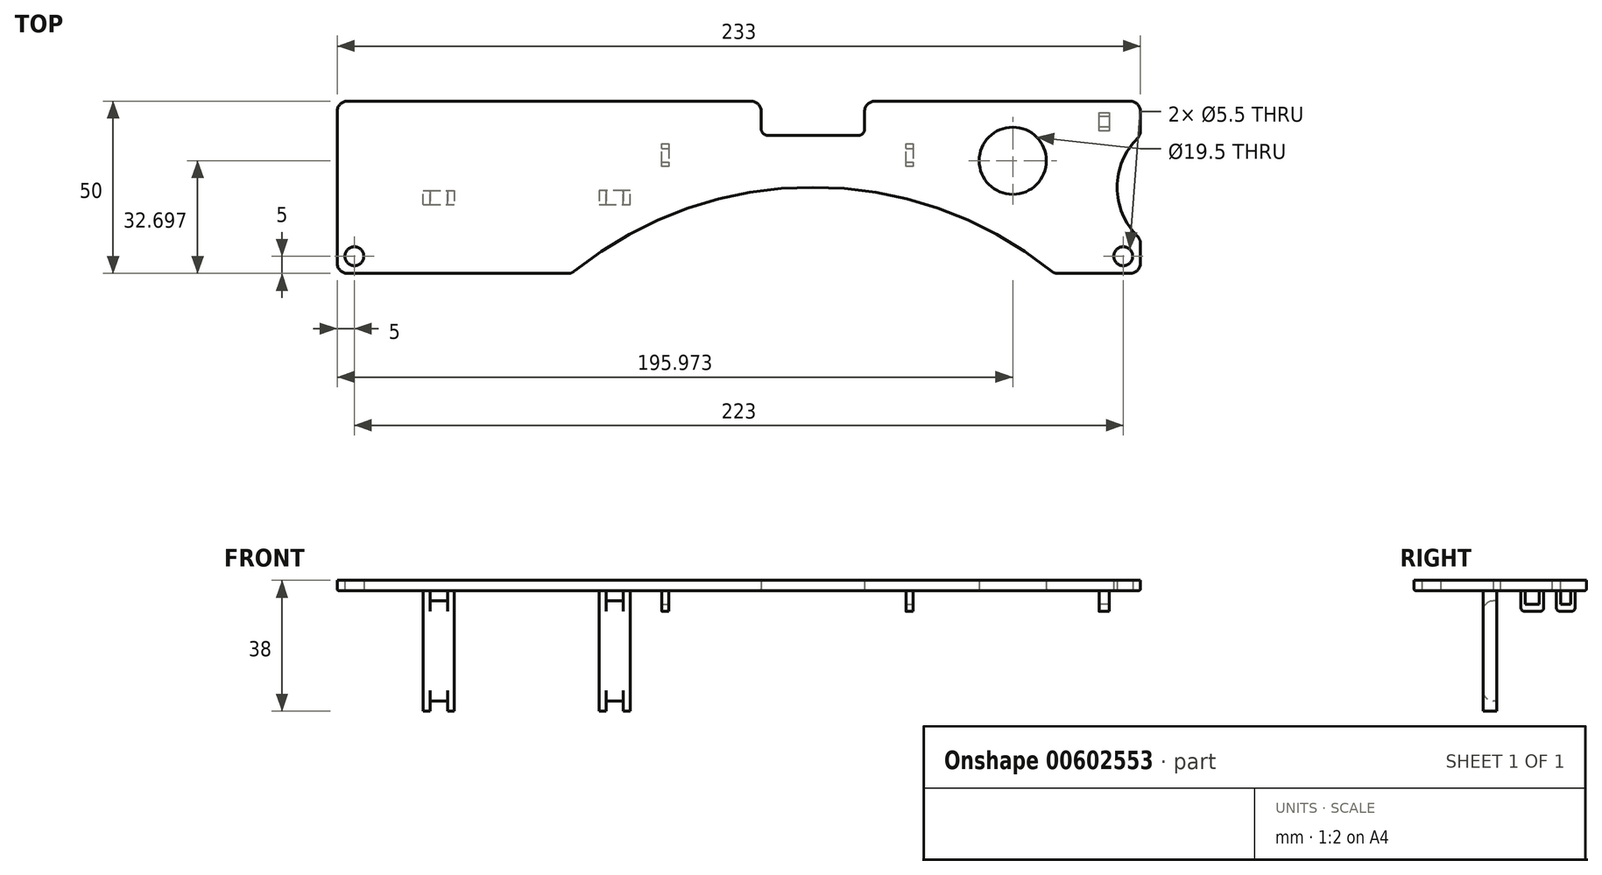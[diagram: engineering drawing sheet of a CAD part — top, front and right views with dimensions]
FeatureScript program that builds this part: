
annotation { "Feature Type Name" : "Feature", "Feature Type Description" : "" }
export const myFeature = defineFeature(function(context is Context, id is Id, definition is map)
    precondition{}
    {
        {
            var Q0;
            Q0=qCreatedBy(makeId("Top.planeOp"),FACE);
            var sketch = newSketch(context, id + "F0", { "sketchPlane" : qUnion([Q0])});
            skLineSegment(sketch, "E0", {"start": v(0, 40) * mm, "end": v(13, 40) * mm});
            skLineSegment(sketch, "E1", {"start": v(15, 42) * mm, "end": v(15, 47) * mm});
            skLineSegment(sketch, "E2", {"start": v(18, 50) * mm, "end": v(85, 50) * mm});
            skLineSegment(sketch, "E3", {"start": v(85, 50) * mm, "end": v(92, 50) * mm});
            skLineSegment(sketch, "E4", {"start": v(92, 0) * mm, "end": v(85, 0) * mm});
            skLineSegment(sketch, "E5", {"start": v(85, 0) * mm, "end": v(71.06, 0) * mm});
            skLineSegment(sketch, "E6", {"start": v(0, 40) * mm, "end": v(-13, 40) * mm});
            skLineSegment(sketch, "E7", {"start": v(-15, 42) * mm, "end": v(-15, 47) * mm});
            skLineSegment(sketch, "E8", {"start": v(-18, 50) * mm, "end": v(-128, 50) * mm});
            skLineSegment(sketch, "E9", {"start": v(-128, 50) * mm, "end": v(-135, 50) * mm});
            skLineSegment(sketch, "E10", {"start": v(-138, 47) * mm, "end": v(-138, 3) * mm});
            skLineSegment(sketch, "E11", {"start": v(-135, 0) * mm, "end": v(-128, 0) * mm});
            skLineSegment(sketch, "E12", {"start": v(-128, 0) * mm, "end": v(-71.06, 0) * mm});
            skArc(sketch, "E13", {"start": v(69.19, 0.66) * mm, "mid": v(0, 25) * mm, "end": v(-69.19, 0.66) * mm});
            skCircle(sketch, "E14", {"center": v(-133, 5) * mm, "radius": 2.75 * mm});
            skCircle(sketch, "E15", {"center": v(90, 5) * mm, "radius": 2.75 * mm});
            skLineSegment(sketch, "E16", {"start": v(95, 3) * mm, "end": v(95, 8.7) * mm});
            skLineSegment(sketch, "E17", {"start": v(95, 47) * mm, "end": v(95, 41.3) * mm});
            skArc(sketch, "E18", {"start": v(94.12, 39.17) * mm, "mid": v(88.23, 25) * mm, "end": v(94.12, 10.83) * mm});
            skPoint(sketch, "E19.visualSharp", {"position": v(-138, 0) * mm});
            skArc(sketch, "E19.filletArc", {"start": v(-138, 3) * mm, "mid": v(-137.12, 0.88) * mm, "end": v(-135, 0) * mm});
            skPoint(sketch, "E20.visualSharp", {"position": v(-138, 50) * mm});
            skArc(sketch, "E20.filletArc", {"start": v(-135, 50) * mm, "mid": v(-137.12, 49.12) * mm, "end": v(-138, 47) * mm});
            skPoint(sketch, "E21.visualSharp", {"position": v(-15, 50) * mm});
            skArc(sketch, "E21.filletArc", {"start": v(-15, 47) * mm, "mid": v(-15.88, 49.12) * mm, "end": v(-18, 50) * mm});
            skPoint(sketch, "E22.visualSharp", {"position": v(15, 50) * mm});
            skArc(sketch, "E22.filletArc", {"start": v(18, 50) * mm, "mid": v(15.88, 49.12) * mm, "end": v(15, 47) * mm});
            skPoint(sketch, "E23.visualSharp", {"position": v(95, 50) * mm});
            skArc(sketch, "E23.filletArc", {"start": v(95, 47) * mm, "mid": v(94.12, 49.12) * mm, "end": v(92, 50) * mm});
            skPoint(sketch, "E24.visualSharp", {"position": v(95, 40) * mm});
            skArc(sketch, "E24.filletArc", {"start": v(94.12, 39.17) * mm, "mid": v(94.77, 40.15) * mm, "end": v(95, 41.3) * mm});
            skPoint(sketch, "E25.visualSharp", {"position": v(95, 10) * mm});
            skArc(sketch, "E25.filletArc", {"start": v(95, 8.7) * mm, "mid": v(94.77, 9.85) * mm, "end": v(94.12, 10.83) * mm});
            skPoint(sketch, "E26.visualSharp", {"position": v(95, 0) * mm});
            skArc(sketch, "E26.filletArc", {"start": v(92, 0) * mm, "mid": v(94.12, 0.88) * mm, "end": v(95, 3) * mm});
            skPoint(sketch, "E27.visualSharp", {"position": v(70, 0) * mm});
            skArc(sketch, "E27.filletArc", {"start": v(69.19, 0.66) * mm, "mid": v(70.07, 0.17) * mm, "end": v(71.06, 0) * mm});
            skPoint(sketch, "E28.visualSharp", {"position": v(-70, 0) * mm});
            skArc(sketch, "E28.filletArc", {"start": v(-71.06, 0) * mm, "mid": v(-70.07, 0.17) * mm, "end": v(-69.19, 0.66) * mm});
            skPoint(sketch, "E29.visualSharp", {"position": v(-15, 40) * mm});
            skArc(sketch, "E29.filletArc", {"start": v(-15, 42) * mm, "mid": v(-14.41, 40.59) * mm, "end": v(-13, 40) * mm});
            skPoint(sketch, "E30.visualSharp", {"position": v(15, 40) * mm});
            skArc(sketch, "E30.filletArc", {"start": v(13, 40) * mm, "mid": v(14.41, 40.59) * mm, "end": v(15, 42) * mm});
            skCircle(sketch, "E31", {"center": v(57.97, 32.7) * mm, "radius": 9.75 * mm});
            skLineSegment(sketch, "E32", {"start": v(-113, 20) * mm, "end": v(-113, 24) * mm});
            skLineSegment(sketch, "E33", {"start": v(-113, 24) * mm, "end": v(-111, 24) * mm});
            skLineSegment(sketch, "E34", {"start": v(-111, 24) * mm, "end": v(-106, 24) * mm});
            skLineSegment(sketch, "E35", {"start": v(-106, 24) * mm, "end": v(-104, 24) * mm});
            skLineSegment(sketch, "E36", {"start": v(-104, 24) * mm, "end": v(-104, 20) * mm});
            skLineSegment(sketch, "E37", {"start": v(-53, 20) * mm, "end": v(-53, 24) * mm});
            skLineSegment(sketch, "E38", {"start": v(-53, 24) * mm, "end": v(-55, 24) * mm});
            skLineSegment(sketch, "E39", {"start": v(-55, 24) * mm, "end": v(-60, 24) * mm});
            skLineSegment(sketch, "E40", {"start": v(-60, 24) * mm, "end": v(-62, 24) * mm});
            skLineSegment(sketch, "E41", {"start": v(-62, 24) * mm, "end": v(-62, 20) * mm});
            skLineSegment(sketch, "E42", {"start": v(-62, 20) * mm, "end": v(-53, 20) * mm});
            skLineSegment(sketch, "E43", {"start": v(-55, 24) * mm, "end": v(-55, 20) * mm});
            skLineSegment(sketch, "E44", {"start": v(-60, 24) * mm, "end": v(-60, 20) * mm});
            skLineSegment(sketch, "E45", {"start": v(-113, 20) * mm, "end": v(-104, 20) * mm});
            skLineSegment(sketch, "E46", {"start": v(-106, 24) * mm, "end": v(-106, 20) * mm});
            skLineSegment(sketch, "E47", {"start": v(-111, 24) * mm, "end": v(-111, 20) * mm});
            skLineSegment(sketch, "E48", {"start": v(27, 31) * mm, "end": v(27, 32.3) * mm});
            skLineSegment(sketch, "E49", {"start": v(-43.79, 31) * mm, "end": v(-43.79, 32.3) * mm});
            skLineSegment(sketch, "E50", {"start": v(-43.79, 32.3) * mm, "end": v(-43.79, 36.3) * mm});
            skLineSegment(sketch, "E51", {"start": v(-43.79, 36.3) * mm, "end": v(-43.79, 37.6) * mm});
            skLineSegment(sketch, "E52", {"start": v(-43.79, 37.6) * mm, "end": v(-41.79, 37.6) * mm});
            skLineSegment(sketch, "E53", {"start": v(27, 32.3) * mm, "end": v(27, 36.3) * mm});
            skLineSegment(sketch, "E54", {"start": v(27, 36.3) * mm, "end": v(27, 37.6) * mm});
            skLineSegment(sketch, "E55", {"start": v(27, 37.6) * mm, "end": v(29, 37.6) * mm});
            skLineSegment(sketch, "E56", {"start": v(29, 37.6) * mm, "end": v(29, 36.3) * mm});
            skLineSegment(sketch, "E57", {"start": v(29, 36.3) * mm, "end": v(29, 32.3) * mm});
            skLineSegment(sketch, "E58", {"start": v(29, 32.3) * mm, "end": v(29, 31) * mm});
            skLineSegment(sketch, "E59", {"start": v(29, 31) * mm, "end": v(27, 31) * mm});
            skLineSegment(sketch, "E60", {"start": v(27, 32.3) * mm, "end": v(29, 32.3) * mm});
            skLineSegment(sketch, "E61", {"start": v(27, 36.3) * mm, "end": v(29, 36.3) * mm});
            skLineSegment(sketch, "E62", {"start": v(-41.79, 37.6) * mm, "end": v(-41.79, 36.3) * mm});
            skLineSegment(sketch, "E63", {"start": v(-41.79, 36.3) * mm, "end": v(-41.79, 32.3) * mm});
            skLineSegment(sketch, "E64", {"start": v(-41.79, 32.3) * mm, "end": v(-41.79, 31) * mm});
            skLineSegment(sketch, "E65", {"start": v(-41.79, 31) * mm, "end": v(-43.79, 31) * mm});
            skLineSegment(sketch, "E66", {"start": v(-43.79, 32.3) * mm, "end": v(-41.79, 32.3) * mm});
            skLineSegment(sketch, "E67", {"start": v(-43.79, 36.3) * mm, "end": v(-41.79, 36.3) * mm});
            skLineSegment(sketch, "E68", {"start": v(86, 41.3) * mm, "end": v(83, 41.3) * mm});
            skLineSegment(sketch, "E69", {"start": v(83, 41.3) * mm, "end": v(83, 42.5) * mm});
            skLineSegment(sketch, "E70", {"start": v(83, 42.5) * mm, "end": v(83, 45.5) * mm});
            skLineSegment(sketch, "E71", {"start": v(83, 45.5) * mm, "end": v(83, 46.7) * mm});
            skLineSegment(sketch, "E72", {"start": v(83, 46.7) * mm, "end": v(86, 46.7) * mm});
            skLineSegment(sketch, "E73", {"start": v(86, 46.7) * mm, "end": v(86, 45.5) * mm});
            skLineSegment(sketch, "E74", {"start": v(86, 45.5) * mm, "end": v(83, 45.5) * mm});
            skLineSegment(sketch, "E75", {"start": v(86, 45.5) * mm, "end": v(86, 42.5) * mm});
            skLineSegment(sketch, "E76", {"start": v(86, 42.5) * mm, "end": v(83, 42.5) * mm});
            skLineSegment(sketch, "E77", {"start": v(86, 42.5) * mm, "end": v(86, 41.3) * mm});
            skLineSegment(sketch, "E78.bottom", {"start": v(-21.5, -115.24) * mm, "end": v(119.92, 26.18) * mm, "construction": true});
            skLineSegment(sketch, "E78.top", {"start": v(-162.92, 26.18) * mm, "end": v(-21.5, 167.6) * mm, "construction": true});
            skLineSegment(sketch, "E78.left", {"start": v(-21.5, -115.24) * mm, "end": v(-162.92, 26.18) * mm, "construction": true});
            skLineSegment(sketch, "E78.right", {"start": v(119.92, 26.18) * mm, "end": v(-21.5, 167.6) * mm, "construction": true});
            skSolve(sketch);
        }
        {
            var Q0;
            Q0=makeQuery(id+"F0.imprint","IMPRINT",FACE,{"disambiguationData":[TD([[makeQuery(id+"F0.imprint","IMPRINT",EDGE,{"derivedFrom":sQuery(id+"F0.wireOp",EDGE,"E0")}),-1.0]])]});
            var Q1;
            Q1=makeQuery(id+"F0.imprint","IMPRINT",FACE,{"disambiguationData":[TD([[makeQuery(id+"F0.imprint","IMPRINT",EDGE,{"derivedFrom":sQuery(id+"F0.wireOp",EDGE,"E34")}),-1.0]])]});
            var Q2;
            {var subQ0=sQuery(id+"F0.wireOp",EDGE,"E32");Q2=makeQuery(id+"F0.imprint","IMPRINT",FACE,{"disambiguationData":[TD([[makeQuery(id+"F0.imprint","IMPRINT",EDGE,{"derivedFrom":subQ0}),-1.0]])]});}
            var Q3;
            Q3=makeQuery(id+"F0.imprint","IMPRINT",FACE,{"disambiguationData":[TD([[makeQuery(id+"F0.imprint","IMPRINT",EDGE,{"derivedFrom":sQuery(id+"F0.wireOp",EDGE,"E35")}),-1.0]])]});
            var Q4;
            Q4=makeQuery(id+"F0.imprint","IMPRINT",FACE,{"disambiguationData":[TD([[makeQuery(id+"F0.imprint","IMPRINT",EDGE,{"derivedFrom":sQuery(id+"F0.wireOp",EDGE,"E39")}),1.0]])]});
            var Q5;
            Q5=makeQuery(id+"F0.imprint","IMPRINT",FACE,{"disambiguationData":[TD([[makeQuery(id+"F0.imprint","IMPRINT",EDGE,{"derivedFrom":sQuery(id+"F0.wireOp",EDGE,"E40")}),1.0]])]});
            var Q6;
            {var subQ0=sQuery(id+"F0.wireOp",EDGE,"E37");Q6=makeQuery(id+"F0.imprint","IMPRINT",FACE,{"disambiguationData":[TD([[makeQuery(id+"F0.imprint","IMPRINT",EDGE,{"derivedFrom":subQ0}),1.0]])]});}
            var Q7;
            {var subQ0=sQuery(id+"F0.wireOp",EDGE,"eKTIc02U-dnFm-GTT2-vQ7b-SwI1Hukl9Nmx");Q7=makeQuery(id+"F0.imprint","IMPRINT",FACE,{"disambiguationData":[TD([[makeQuery(id+"F0.imprint","IMPRINT",EDGE,{"derivedFrom":subQ0}),1.0]])]});}
            var Q8;
            {var subQ2=sQuery(id+"F0.wireOp",EDGE,"1qOz53Yj-txPT-SCg7-ZgNw-TuK4SumJtAh8");Q8=makeQuery(id+"F0.imprint","IMPRINT",FACE,{"disambiguationData":[TD([[makeQuery(id+"F0.imprint","IMPRINT",EDGE,{"derivedFrom":subQ2}),1.0]])]});}
            var Q9;
            {var subQ0=sQuery(id+"F0.wireOp",EDGE,"QpRtkNc5-8LMi-cX35-Ux5E-ZP7ejwDYLjvo");Q9=makeQuery(id+"F0.imprint","IMPRINT",FACE,{"disambiguationData":[TD([[makeQuery(id+"F0.imprint","IMPRINT",EDGE,{"derivedFrom":subQ0}),-1.0]])]});}
            var Q10;
            Q10=makeQuery(id+"F0.imprint","IMPRINT",FACE,{"disambiguationData":[TD([[makeQuery(id+"F0.imprint","IMPRINT",EDGE,{"derivedFrom":sQuery(id+"F0.wireOp",EDGE,"E50")}),-1.0]])]});
            var Q11;
            Q11=makeQuery(id+"F0.imprint","IMPRINT",FACE,{"disambiguationData":[TD([[makeQuery(id+"F0.imprint","IMPRINT",EDGE,{"derivedFrom":sQuery(id+"F0.wireOp",EDGE,"E49")}),-1.0]])]});
            var Q12;
            Q12=makeQuery(id+"F0.imprint","IMPRINT",FACE,{"disambiguationData":[TD([[makeQuery(id+"F0.imprint","IMPRINT",EDGE,{"derivedFrom":sQuery(id+"F0.wireOp",EDGE,"E51")}),-1.0]])]});
            var Q13;
            Q13=makeQuery(id+"F0.imprint","IMPRINT",FACE,{"disambiguationData":[TD([[makeQuery(id+"F0.imprint","IMPRINT",EDGE,{"derivedFrom":sQuery(id+"F0.wireOp",EDGE,"E53")}),-1.0]])]});
            var Q14;
            Q14=makeQuery(id+"F0.imprint","IMPRINT",FACE,{"disambiguationData":[TD([[makeQuery(id+"F0.imprint","IMPRINT",EDGE,{"derivedFrom":sQuery(id+"F0.wireOp",EDGE,"E48")}),-1.0]])]});
            var Q15;
            Q15=makeQuery(id+"F0.imprint","IMPRINT",FACE,{"disambiguationData":[TD([[makeQuery(id+"F0.imprint","IMPRINT",EDGE,{"derivedFrom":sQuery(id+"F0.wireOp",EDGE,"E54")}),-1.0]])]});
            var Q16;
            Q16=makeQuery(id+"F0.imprint","IMPRINT",FACE,{"disambiguationData":[TD([[makeQuery(id+"F0.imprint","IMPRINT",EDGE,{"derivedFrom":sQuery(id+"F0.wireOp",EDGE,"E70")}),-1.0]])]});
            var Q17;
            Q17=makeQuery(id+"F0.imprint","IMPRINT",FACE,{"disambiguationData":[TD([[makeQuery(id+"F0.imprint","IMPRINT",EDGE,{"derivedFrom":sQuery(id+"F0.wireOp",EDGE,"E71")}),-1.0]])]});
            var Q18;
            Q18=makeQuery(id+"F0.imprint","IMPRINT",FACE,{"disambiguationData":[TD([[makeQuery(id+"F0.imprint","IMPRINT",EDGE,{"derivedFrom":sQuery(id+"F0.wireOp",EDGE,"E68")}),-1.0]])]});
            extrude(context, id + "F1", {"entities" : qUnion([Q0, Q1, Q2, Q3, Q4, Q5, Q6, Q7, Q8, Q9, Q10, Q11, Q12, Q13, Q14, Q15, Q16, Q17, Q18]), "flatOperationType" : FlatOperationType.REMOVE, "depth" : 3 * mm, "offsetDistance" : 25 * mm, "domain" : OperationDomain.MODEL});
        }
        {
            var Q0;
            Q0=makeQuery(id+"F0.imprint","IMPRINT",FACE,{"disambiguationData":[TD([[makeQuery(id+"F0.imprint","IMPRINT",EDGE,{"derivedFrom":sQuery(id+"F0.wireOp",EDGE,"E51")}),-1.0]])]});
            var Q1;
            Q1=makeQuery(id+"F0.imprint","IMPRINT",FACE,{"disambiguationData":[TD([[makeQuery(id+"F0.imprint","IMPRINT",EDGE,{"derivedFrom":sQuery(id+"F0.wireOp",EDGE,"E49")}),-1.0]])]});
            var Q2;
            Q2=makeQuery(id+"F0.imprint","IMPRINT",FACE,{"disambiguationData":[TD([[makeQuery(id+"F0.imprint","IMPRINT",EDGE,{"derivedFrom":sQuery(id+"F0.wireOp",EDGE,"E48")}),-1.0]])]});
            var Q3;
            Q3=makeQuery(id+"F0.imprint","IMPRINT",FACE,{"disambiguationData":[TD([[makeQuery(id+"F0.imprint","IMPRINT",EDGE,{"derivedFrom":sQuery(id+"F0.wireOp",EDGE,"E54")}),-1.0]])]});
            extrude(context, id + "F2", {"entities" : qUnion([Q0, Q1, Q2, Q3]), "operationType" : NewBodyOperationType.ADD, "oppositeDirection" : true, "depth" : 4 * mm, "offsetDistance" : 25 * mm});
        }
        {
            var Q0;
            Q0=makeQuery(id+"F0.imprint","IMPRINT",FACE,{"disambiguationData":[TD([[makeQuery(id+"F0.imprint","IMPRINT",EDGE,{"derivedFrom":sQuery(id+"F0.wireOp",EDGE,"E50")}),-1.0]])]});
            var Q1;
            Q1=makeQuery(id+"F0.imprint","IMPRINT",FACE,{"disambiguationData":[TD([[makeQuery(id+"F0.imprint","IMPRINT",EDGE,{"derivedFrom":sQuery(id+"F0.wireOp",EDGE,"E51")}),-1.0]])]});
            var Q2;
            Q2=makeQuery(id+"F0.imprint","IMPRINT",FACE,{"disambiguationData":[TD([[makeQuery(id+"F0.imprint","IMPRINT",EDGE,{"derivedFrom":sQuery(id+"F0.wireOp",EDGE,"E49")}),-1.0]])]});
            var Q3;
            Q3=makeQuery(id+"F0.imprint","IMPRINT",FACE,{"disambiguationData":[TD([[makeQuery(id+"F0.imprint","IMPRINT",EDGE,{"derivedFrom":sQuery(id+"F0.wireOp",EDGE,"E53")}),-1.0]])]});
            var Q4;
            Q4=makeQuery(id+"F0.imprint","IMPRINT",FACE,{"disambiguationData":[TD([[makeQuery(id+"F0.imprint","IMPRINT",EDGE,{"derivedFrom":sQuery(id+"F0.wireOp",EDGE,"E54")}),-1.0]])]});
            var Q5;
            Q5=makeQuery(id+"F0.imprint","IMPRINT",FACE,{"disambiguationData":[TD([[makeQuery(id+"F0.imprint","IMPRINT",EDGE,{"derivedFrom":sQuery(id+"F0.wireOp",EDGE,"E48")}),-1.0]])]});
            extrude(context, id + "F3", {"entities" : qUnion([Q0, Q1, Q2, Q3, Q4, Q5]), "operationType" : NewBodyOperationType.ADD, "oppositeDirection" : true, "depth" : 6 * mm, "offsetDistance" : 25 * mm, "hasSecondDirection" : true, "secondDirectionOppositeDirection" : true, "secondDirectionDepth" : 4 * mm});
        }
        {
            var Q0;
            {var subQ0=sQuery(id+"F0.wireOp",EDGE,"E32");Q0=makeQuery(id+"F0.imprint","IMPRINT",FACE,{"disambiguationData":[TD([[makeQuery(id+"F0.imprint","IMPRINT",EDGE,{"derivedFrom":subQ0}),-1.0]])]});}
            var Q1;
            Q1=makeQuery(id+"F0.imprint","IMPRINT",FACE,{"disambiguationData":[TD([[makeQuery(id+"F0.imprint","IMPRINT",EDGE,{"derivedFrom":sQuery(id+"F0.wireOp",EDGE,"E35")}),-1.0]])]});
            var Q2;
            Q2=makeQuery(id+"F0.imprint","IMPRINT",FACE,{"disambiguationData":[TD([[makeQuery(id+"F0.imprint","IMPRINT",EDGE,{"derivedFrom":sQuery(id+"F0.wireOp",EDGE,"E40")}),1.0]])]});
            var Q3;
            {var subQ0=sQuery(id+"F0.wireOp",EDGE,"E37");Q3=makeQuery(id+"F0.imprint","IMPRINT",FACE,{"disambiguationData":[TD([[makeQuery(id+"F0.imprint","IMPRINT",EDGE,{"derivedFrom":subQ0}),1.0]])]});}
            extrude(context, id + "F4", {"entities" : qUnion([Q0, Q1, Q2, Q3]), "operationType" : NewBodyOperationType.ADD, "oppositeDirection" : true, "depth" : 35 * mm, "offsetDistance" : 25 * mm});
        }
        {
            var Q0;
            Q0=makeQuery(id+"F0.imprint","IMPRINT",FACE,{"disambiguationData":[TD([[makeQuery(id+"F0.imprint","IMPRINT",EDGE,{"derivedFrom":sQuery(id+"F0.wireOp",EDGE,"E34")}),-1.0]])]});
            var Q1;
            Q1=makeQuery(id+"F0.imprint","IMPRINT",FACE,{"disambiguationData":[TD([[makeQuery(id+"F0.imprint","IMPRINT",EDGE,{"derivedFrom":sQuery(id+"F0.wireOp",EDGE,"E39")}),1.0]])]});
            extrude(context, id + "F5", {"entities" : qUnion([Q0, Q1]), "operationType" : NewBodyOperationType.ADD, "oppositeDirection" : true, "depth" : 32 * mm, "offsetDistance" : 25 * mm, "hasSecondDirection" : true, "secondDirectionOppositeDirection" : true, "secondDirectionDepth" : (3) * mm});
        }
        {
            var Q0;
            Q0=makeQuery(id+"F5.opExtrude","CAP_EDGE",EDGE,{"disambiguationData":[OSD([sQuery(id+"F0.wireOp",EDGE,"E42")])],"isStart":false});
            var Q1;
            Q1=makeQuery(id+"F5.opExtrude","CAP_EDGE",EDGE,{"disambiguationData":[OSD([sQuery(id+"F0.wireOp",EDGE,"E42")])],"isStart":true});
            var Q2;
            Q2=makeQuery(id+"F5.opExtrude","CAP_EDGE",EDGE,{"disambiguationData":[OSD([sQuery(id+"F0.wireOp",EDGE,"E45")])],"isStart":false});
            var Q3;
            Q3=makeQuery(id+"F5.opExtrude","CAP_EDGE",EDGE,{"disambiguationData":[OSD([sQuery(id+"F0.wireOp",EDGE,"E45")])],"isStart":true});
            fillet(context, id + "F6", {"entities" : qUnion([Q0, Q1, Q2, Q3]), "radius" : 3 * mm, "tangentPropagation" : true, "allowEdgeOverflow" : false});
        }
        {
            var Q0;
            Q0=makeQuery(id+"F1.opExtrude","CAP_EDGE",EDGE,{"disambiguationData":[OSD([sQuery(id+"F0.wireOp",EDGE,"E11"),sQuery(id+"F0.wireOp",EDGE,"E12")])],"isStart":true});
            var Q1;
            Q1=makeQuery(id+"F1.opExtrude","CAP_EDGE",EDGE,{"disambiguationData":[OSD([sQuery(id+"F0.wireOp",EDGE,"E14")])],"isStart":true});
            var Q2;
            Q2=makeQuery(id+"F1.opExtrude","CAP_EDGE",EDGE,{"disambiguationData":[OSD([sQuery(id+"F0.wireOp",EDGE,"E31")])],"isStart":true});
            var Q3;
            Q3=makeQuery(id+"F1.opExtrude","CAP_EDGE",EDGE,{"disambiguationData":[OSD([sQuery(id+"F0.wireOp",EDGE,"E15")])],"isStart":true});
            var Q4;
            Q4=makeQuery(id+"F5.opExtrude","CAP_EDGE",EDGE,{"disambiguationData":[OSD([sQuery(id+"F0.wireOp",EDGE,"E39")])],"isStart":false});
            var Q5;
            Q5=makeQuery(id+"F5.opExtrude","CAP_EDGE",EDGE,{"disambiguationData":[OSD([sQuery(id+"F0.wireOp",EDGE,"E39")])],"isStart":true});
            var Q6;
            Q6=makeQuery(id+"F5.opExtrude","CAP_EDGE",EDGE,{"disambiguationData":[OSD([sQuery(id+"F0.wireOp",EDGE,"E34")])],"isStart":true});
            var Q7;
            Q7=makeQuery(id+"F5.opExtrude","CAP_EDGE",EDGE,{"disambiguationData":[OSD([sQuery(id+"F0.wireOp",EDGE,"E34")])],"isStart":false});
            fillet(context, id + "F7", {"entities" : qUnion([Q0, Q1, Q2, Q3, Q4, Q5, Q6, Q7]), "radius" : 0.5 * mm, "tangentPropagation" : true, "allowEdgeOverflow" : false});
        }
        {
            var Q0;
            Q0=makeQuery(id+"F2.opExtrude","CAP_EDGE",EDGE,{"disambiguationData":[OSD([sQuery(id+"F0.wireOp",EDGE,"E66")])],"isStart":true});
            var Q1;
            Q1=makeQuery(id+"F2.opExtrude","CAP_EDGE",EDGE,{"disambiguationData":[OSD([sQuery(id+"F0.wireOp",EDGE,"E67")])],"isStart":true});
            var Q2;
            Q2=makeQuery(id+"F2.opExtrude","CAP_EDGE",EDGE,{"disambiguationData":[OSD([sQuery(id+"F0.wireOp",EDGE,"E60")])],"isStart":true});
            var Q3;
            Q3=makeQuery(id+"F2.opExtrude","CAP_EDGE",EDGE,{"disambiguationData":[OSD([sQuery(id+"F0.wireOp",EDGE,"E67")])],"isStart":false});
            var Q4;
            Q4=makeQuery(id+"F2.opExtrude","CAP_EDGE",EDGE,{"disambiguationData":[OSD([sQuery(id+"F0.wireOp",EDGE,"E66")])],"isStart":false});
            var Q5;
            Q5=makeQuery(id+"F2.opExtrude","CAP_EDGE",EDGE,{"disambiguationData":[OSD([sQuery(id+"F0.wireOp",EDGE,"E60")])],"isStart":false});
            var Q6;
            Q6=makeQuery(id+"F2.opExtrude","CAP_EDGE",EDGE,{"disambiguationData":[OSD([sQuery(id+"F0.wireOp",EDGE,"E61")])],"isStart":true});
            var Q7;
            Q7=makeQuery(id+"F2.opExtrude","CAP_EDGE",EDGE,{"disambiguationData":[OSD([sQuery(id+"F0.wireOp",EDGE,"E61")])],"isStart":false});
            var Q8;
            Q8=makeQuery(id+"F3.opExtrude","CAP_EDGE",EDGE,{"disambiguationData":[OSD([sQuery(id+"F0.wireOp",EDGE,"E59")])],"isStart":false});
            var Q9;
            Q9=makeQuery(id+"F3.opExtrude","CAP_EDGE",EDGE,{"disambiguationData":[OSD([sQuery(id+"F0.wireOp",EDGE,"E55")])],"isStart":false});
            var Q10;
            Q10=makeQuery(id+"F2.opExtrude","CAP_EDGE",EDGE,{"disambiguationData":[OSD([sQuery(id+"F0.wireOp",EDGE,"E55")])],"isStart":true});
            var Q11;
            Q11=makeQuery(id+"F2.opExtrude","CAP_EDGE",EDGE,{"disambiguationData":[OSD([sQuery(id+"F0.wireOp",EDGE,"E59")])],"isStart":true});
            var Q12;
            Q12=makeQuery(id+"F3.opExtrude","CAP_EDGE",EDGE,{"disambiguationData":[OSD([sQuery(id+"F0.wireOp",EDGE,"E52")])],"isStart":false});
            var Q13;
            Q13=makeQuery(id+"F2.opExtrude","CAP_EDGE",EDGE,{"disambiguationData":[OSD([sQuery(id+"F0.wireOp",EDGE,"E52")])],"isStart":true});
            var Q14;
            Q14=makeQuery(id+"F2.opExtrude","CAP_EDGE",EDGE,{"disambiguationData":[OSD([sQuery(id+"F0.wireOp",EDGE,"E65")])],"isStart":true});
            var Q15;
            Q15=makeQuery(id+"F3.opExtrude","CAP_EDGE",EDGE,{"disambiguationData":[OSD([sQuery(id+"F0.wireOp",EDGE,"E65")])],"isStart":false});
            var Q16;
            Q16=makeQuery(id+"F4.opExtrude","CAP_EDGE",EDGE,{"disambiguationData":[OSD([sQuery(id+"F0.wireOp",EDGE,"E41")])],"isStart":true});
            var Q17;
            Q17=makeQuery(id+"F4.opExtrude","CAP_EDGE",EDGE,{"disambiguationData":[OSD([sQuery(id+"F0.wireOp",EDGE,"E37")])],"isStart":true});
            var Q18;
            Q18=makeQuery(id+"F4.opExtrude","CAP_EDGE",EDGE,{"disambiguationData":[OSD([sQuery(id+"F0.wireOp",EDGE,"E32")])],"isStart":true});
            var Q19;
            Q19=makeQuery(id+"F4.opExtrude","CAP_EDGE",EDGE,{"disambiguationData":[OSD([sQuery(id+"F0.wireOp",EDGE,"E36")])],"isStart":true});
            fillet(context, id + "F8", {"entities" : qUnion([Q0, Q1, Q2, Q3, Q4, Q5, Q6, Q7, Q8, Q9, Q10, Q11, Q12, Q13, Q14, Q15, Q16, Q17, Q18, Q19]), "radius" : 1 * mm, "tangentPropagation" : true, "allowEdgeOverflow" : false});
        }
        {
            var Q0;
            Q0=makeQuery(id+"F0.imprint","IMPRINT",FACE,{"disambiguationData":[TD([[makeQuery(id+"F0.imprint","IMPRINT",EDGE,{"derivedFrom":sQuery(id+"F0.wireOp",EDGE,"E68")}),-1.0]])]});
            var Q1;
            Q1=makeQuery(id+"F0.imprint","IMPRINT",FACE,{"disambiguationData":[TD([[makeQuery(id+"F0.imprint","IMPRINT",EDGE,{"derivedFrom":sQuery(id+"F0.wireOp",EDGE,"E71")}),-1.0]])]});
            extrude(context, id + "F9", {"entities" : qUnion([Q0, Q1]), "operationType" : NewBodyOperationType.ADD, "oppositeDirection" : true, "depth" : 4 * mm, "offsetDistance" : 25 * mm});
        }
        {
            var Q0;
            Q0=makeQuery(id+"F0.imprint","IMPRINT",FACE,{"disambiguationData":[TD([[makeQuery(id+"F0.imprint","IMPRINT",EDGE,{"derivedFrom":sQuery(id+"F0.wireOp",EDGE,"E70")}),-1.0]])]});
            var Q1;
            Q1=makeQuery(id+"F0.imprint","IMPRINT",FACE,{"disambiguationData":[TD([[makeQuery(id+"F0.imprint","IMPRINT",EDGE,{"derivedFrom":sQuery(id+"F0.wireOp",EDGE,"E68")}),-1.0]])]});
            var Q2;
            Q2=makeQuery(id+"F0.imprint","IMPRINT",FACE,{"disambiguationData":[TD([[makeQuery(id+"F0.imprint","IMPRINT",EDGE,{"derivedFrom":sQuery(id+"F0.wireOp",EDGE,"E71")}),-1.0]])]});
            extrude(context, id + "F10", {"entities" : qUnion([Q0, Q1, Q2]), "operationType" : NewBodyOperationType.ADD, "oppositeDirection" : true, "depth" : 6 * mm, "offsetDistance" : 25 * mm, "hasSecondDirection" : true, "secondDirectionOppositeDirection" : true, "secondDirectionDepth" : 4 * mm});
        }
        {
            var Q0;
            Q0=makeQuery(id+"F10.opExtrude","CAP_EDGE",EDGE,{"disambiguationData":[OSD([sQuery(id+"F0.wireOp",EDGE,"E68")])],"isStart":false});
            var Q1;
            Q1=makeQuery(id+"F10.opExtrude","CAP_EDGE",EDGE,{"disambiguationData":[OSD([sQuery(id+"F0.wireOp",EDGE,"E72")])],"isStart":false});
            var Q2;
            Q2=makeQuery(id+"F9.opExtrude","CAP_EDGE",EDGE,{"disambiguationData":[OSD([sQuery(id+"F0.wireOp",EDGE,"E76")])],"isStart":false});
            var Q3;
            Q3=makeQuery(id+"F9.opExtrude","CAP_EDGE",EDGE,{"disambiguationData":[OSD([sQuery(id+"F0.wireOp",EDGE,"E74")])],"isStart":false});
            var Q4;
            Q4=makeQuery(id+"F9.opExtrude","CAP_EDGE",EDGE,{"disambiguationData":[OSD([sQuery(id+"F0.wireOp",EDGE,"E74")])],"isStart":true});
            var Q5;
            Q5=makeQuery(id+"F9.opExtrude","CAP_EDGE",EDGE,{"disambiguationData":[OSD([sQuery(id+"F0.wireOp",EDGE,"E76")])],"isStart":true});
            var Q6;
            Q6=makeQuery(id+"F9.opExtrude","CAP_EDGE",EDGE,{"disambiguationData":[OSD([sQuery(id+"F0.wireOp",EDGE,"E68")])],"isStart":true});
            var Q7;
            Q7=makeQuery(id+"F9.opExtrude","CAP_EDGE",EDGE,{"disambiguationData":[OSD([sQuery(id+"F0.wireOp",EDGE,"E72")])],"isStart":true});
            fillet(context, id + "F11", {"entities" : qUnion([Q0, Q1, Q2, Q3, Q4, Q5, Q6, Q7]), "radius" : 1 * mm, "tangentPropagation" : true, "allowEdgeOverflow" : false});
        }
    });
